# Revit family: 07772203
name_source: partatom
category: Plumbing Fixtures
revit_build: Autodesk Revit 2017 (Build: 20181011_1645(x64)
units: mm (PartAtom-declared; Revit-internal decimal feet)

## family parameters
Always vertical = Yes
Cut with Voids When Loaded = No
OmniClass Number = 23.45.55.00
OmniClass Title = Sanitary Faucets, Wastes
Part Type = Normal
Room Calculation Point = No
Round Connector Dimension = Use Diameter
Shared = No
Work Plane-Based = No

## types (1)
- 07772203 Kitchen faucet with dishwasher valve, 230/12 V
    2D/3D/BIM Files URL = http://static.hansa.com
    Advanced Features = Adjustable settings (with magnetic key)
    Aerator = CACHÉ® integrated aerator;CASCADE®
    AssetType = Fixed
    Automatic Flush = off (off/12/24/48/72 h)
    Automatic Flush Period = 30 s (10-600 s)
    BIMObjectName = 07772203
    BodyMaterial = Brass
    Brand = Hansa
    Catalog Drawing URL = http://static.hansa.com
    Category = Kitchen
    Class = Tiptronic, plug transformer
    CloseOffRating = 0
    Color = Chrome/White
    Connection = Flexible Inlet Pipes
    Connection Size = G3/8
    ConvergoRefNr = 0087-1906-0050-FI
    Customs Code = 84818011
    DN Size = DN15
    Dimension Drawing URL = http://static.hansa.com
    Dishwasher Valve = Electronic dishwasher valve
    Dishwasher Valve Open Period = 4 h / 12 h
    DurationUnit = Year
    EAN Number = 4015470030439
    EMC Directive = 2004/108/EY
    Electrical Connection = 230 / 12 V
    Electronic Parts = Signal lights;Control unit
    FDV Document URL = http://www.hansa.com
    FaucetMainMaterial = Brass
    Features = Tiptronic, plug transformer
    Finish = Polished
    Flow Drawing URL = http://static.hansa.com
    Flow Rate At 300kPa = 0.1 L/s
    FlowCoefficient = 0
    Group = Kitchen faucets
    IfcExportAs = IfcValveType
    IfcExportType = FAUCET
    InletConnectionSize = 10 mm  [stored 0.0328084 ft]
    Installation Type = Deck mounted
    Installation and Maintenance = http://static.hansa.com
    Lever Handle = Temperature control handle;Flow control handle
    ManufacterURL = http://www.hansa.com
    Manufacturer = Hansa
    ManufacturerName = Hansa
    Market = AUT;BEL;DEU;ESP;FRA;INT;ITA;NLD
    Material = Brass
    Max Flow Period = 6.0 s
    Max. Hot Water Supply = 70 °C
    Model = 07772203 Kitchen faucet with dishwasher valve, 230/12 V
    ModelReference = 07772203
    Mounting Holes = 1 mounting hole
    NBSDescription = Water supply fittings for wash basin and troughs
    NBSReference = 45-35-70/371
    Name = 07772203 Kitchen faucet with dishwasher valve, 230/12 V
    Name_en = 07772203 Kitchen faucet with dishwasher valve, 230/12 V
    Noise Class = I (ISO 3822)
    NominalDepth = 254 mm
    NominalHeight = 302 mm
    NominalWidth = 80 mm  [stored 0.262467 ft]
    Operating Voltage = 12 V
    Package Weight = 3.762 kg
    Package external Dimensions = 693 x 177 x 92
    Pipes = Flexible inlet pipe(s)
    Product Code = 07772203
    Product Datasheet = http://www.hansa.com
    Product Family = ALESSI Sense by HANSA
    Product Image URL = http://static.hansa.com
    Product URL = http://static.hansa.com
    Projection = 200 mm  [stored 0.656168 ft]
    Protection Class = IP 44
    Safety Sales Arguments = Valve for shutting off the water inlet for a dishwasher or washing machine at the fitting.
    Shape = Sculptured
    Size = 80x255x300 mm
    Spare Parts = http://static.hansa.com
    Spout Swivel Range = 110° (85° / 60°)
    Spout Type = Swivel spout
    Uniclass2 = Pr_40_30_96_45
    Uniclass2015Description = Sink manual water supply sets
    Uniclass2015Reference = Pr_40_20_87_82
    Version = 1
    VersionDate = 12/06/2019
    WarrantyDescription = http://warranty.hansa.com
    WarrantyDurationUnit = Year
    WorkingPressure = 100- 1000 kPa

note: [stored X ft] marks values corroborated as IEEE doubles in the binary element streams (Revit-internal decimal feet)

## geometry (parser evidence)
native form markers: Sweep x6
no freeform markers — native parametric forms only
